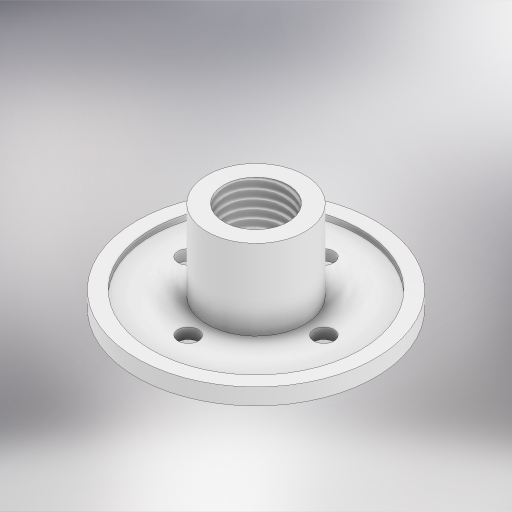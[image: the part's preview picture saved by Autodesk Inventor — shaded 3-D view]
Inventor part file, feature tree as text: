
AUTODESK INVENTOR PART (.ipt)
format: ipt  version: 2023 (Build 270158000, 158)  size: 355,328 bytes
history: native  units: mm
features: extrude x5, sketch x4, other x1, thread x1
ambient origin geometry x8: Origin, YZ Plane, XZ Plane, XY Plane, X Axis, Y Axis, Z Axis, Center Point
bodies: Body1 (feature_tree)
feature tree (11):
  other  "Sólido1"
  sketch  "Boceto1"  dims[d0=70.33mm d1=18.97mm]
  extrude  "Extrusión1"  Depth=18.97mm
  extrude  "Extrusión2"  Depth=26.85mm TaperAngle=0.0deg
  thread  "Rosca1"  [1 undecoded]
  extrude  "Extrusión3"  Depth=61.67mm
  extrude  "Extrusión4"  Depth=10.0mm TaperAngle=0.0deg
  extrude  "Extrusión5"  Depth=26.85mm
  sketch  "Boceto2"  dims[d2=28.9mm d3=26.85mm d4=0.0mm d5=4.85mm d6=0.0mm]
  sketch  "Boceto3"  dims[d7=21.97mm d8=0.0mm d9=61.67mm]
  sketch  "Boceto4"  dims[d10=1.67mm d11=0.0mm d12=10.0mm d13=0.0mm d14=6.0mm d15=20.0mm d16=0.0mm d17=40.0mm d19=360.0deg d21=26.85mm d22=0.0mm]
note: 1 required parameter value undecoded (feature->parameter linkage not recoverable at this tier; creation-order binding heuristic only, values carry confidence <= 0.55)
